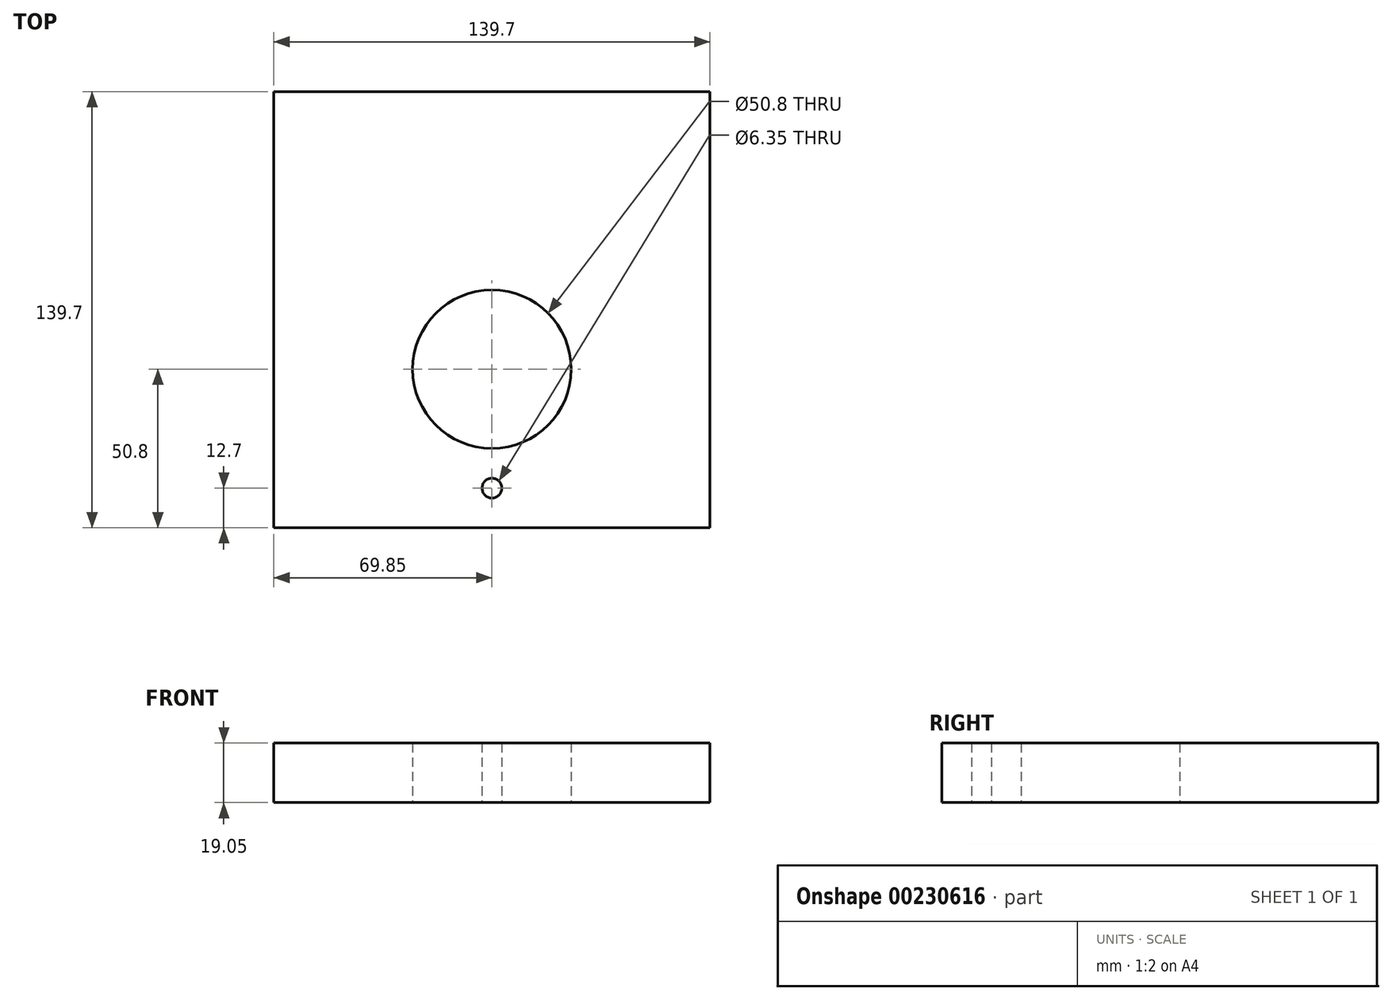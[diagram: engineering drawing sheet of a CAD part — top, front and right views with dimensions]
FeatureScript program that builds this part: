
annotation { "Feature Type Name" : "Feature", "Feature Type Description" : "" }
export const myFeature = defineFeature(function(context is Context, id is Id, definition is map)
    precondition{}
    {
        {
            var Q0;
            Q0=qCreatedBy(makeId("Top.planeOp"),FACE);
            var sketch = newSketch(context, id + "F0", { "sketchPlane" : qUnion([Q0])});
            skLineSegment(sketch, "E0.bottom", {"start": v(-69.85, 69.85) * mm, "end": v(69.85, 69.85) * mm});
            skLineSegment(sketch, "E0.top", {"start": v(-69.85, -69.85) * mm, "end": v(69.85, -69.85) * mm});
            skLineSegment(sketch, "E0.left", {"start": v(-69.85, 69.85) * mm, "end": v(-69.85, -69.85) * mm});
            skLineSegment(sketch, "E0.right", {"start": v(69.85, 69.85) * mm, "end": v(69.85, -69.85) * mm});
            skPoint(sketch, "E0.middle", {"position": v(0, 0) * mm});
            skPoint(sketch, "E1.endSnap0", {"position": v(0, -69.85) * mm});
            skCircle(sketch, "E2", {"center": v(0, -19.05) * mm, "radius": 25.4 * mm});
            skCircle(sketch, "E3", {"center": v(0, -57.15) * mm, "radius": 3.18 * mm});
            skSolve(sketch);
        }
        {
            var Q0;
            Q0=makeQuery(id+"F0.imprint","IMPRINT",FACE,{"disambiguationData":[TD([[makeQuery(id+"F0.imprint","IMPRINT",EDGE,{"derivedFrom":sQuery(id+"F0.wireOp",EDGE,"E0.bottom")}),-1.0]])]});
            extrude(context, id + "F1", {"entities" : qUnion([Q0]), "depth" : 19.05 * mm});
        }
    });
